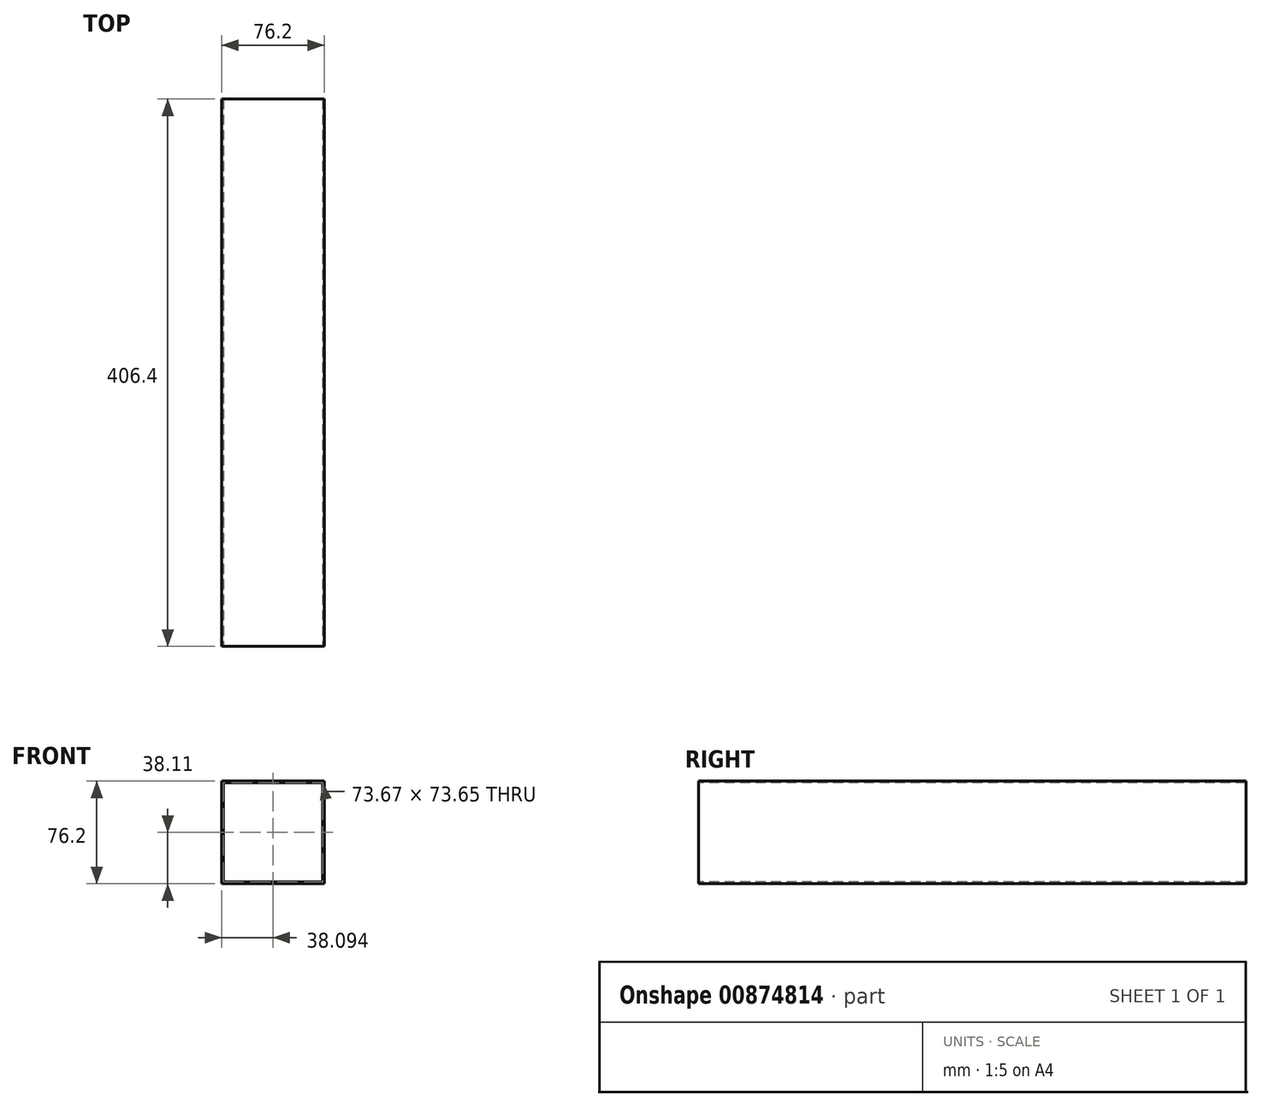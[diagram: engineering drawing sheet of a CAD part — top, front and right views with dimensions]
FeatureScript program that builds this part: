
annotation { "Feature Type Name" : "Feature", "Feature Type Description" : "" }
export const myFeature = defineFeature(function(context is Context, id is Id, definition is map)
    precondition{}
    {
        {
            var Q0;
            Q0=qCreatedBy(makeId("Front.planeOp"),FACE);
            var sketch = newSketch(context, id + "F0", { "sketchPlane" : qUnion([Q0])});
            skLineSegment(sketch, "E0.bottom", {"start": v(-117.25, 89.57) * mm, "end": v(-41.05, 89.57) * mm});
            skLineSegment(sketch, "E0.top", {"start": v(-117.25, 13.37) * mm, "end": v(-41.05, 13.37) * mm});
            skLineSegment(sketch, "E0.left", {"start": v(-117.25, 89.57) * mm, "end": v(-117.25, 13.37) * mm});
            skLineSegment(sketch, "E0.right", {"start": v(-41.05, 89.57) * mm, "end": v(-41.05, 13.37) * mm});
            skSolve(sketch);
        }
        {
            var Q0;
            Q0=qSketchRegion(id+"F0",true);
            extrude(context, id + "F1", {"entities" : qUnion([Q0]), "depth" : 609.6 * mm, "offsetDistance" : 25.4 * mm});
        }
        {
            var Q0;
            Q0=makeQuery(id+"F1.opExtrude","CAP_FACE",FACE,{"disambiguationData":[OSD([sQuery(id+"F0.wireOp",EDGE,"E0.bottom"),sQuery(id+"F0.wireOp",EDGE,"E0.top"),sQuery(id+"F0.wireOp",EDGE,"E0.left"),sQuery(id+"F0.wireOp",EDGE,"E0.right")])],"isStart":false});
            var sketch = newSketch(context, id + "F2", { "sketchPlane" : qUnion([Q0])});
            skLineSegment(sketch, "E1", {"start": v(-98.69, 89.57) * mm, "end": v(-98.69, 88.3) * mm});
            skLineSegment(sketch, "E2", {"start": v(-98.69, 88.3) * mm, "end": v(-116, 88.3) * mm});
            skLineSegment(sketch, "E3", {"start": v(-116, 88.3) * mm, "end": v(-116, 14.66) * mm});
            skLineSegment(sketch, "E4", {"start": v(-116, 14.66) * mm, "end": v(-42.32, 14.66) * mm});
            skLineSegment(sketch, "E5", {"start": v(-42.32, 14.66) * mm, "end": v(-42.32, 88.3) * mm});
            skLineSegment(sketch, "E6", {"start": v(-42.32, 88.3) * mm, "end": v(-98.69, 88.3) * mm});
            skSolve(sketch);
        }
        {
            var Q0;
            Q0=makeQuery(id+"F2.imprint","IMPRINT",FACE,{"disambiguationData":[TD([[makeQuery(id+"F2.imprint","IMPRINT",EDGE,{"derivedFrom":sQuery(id+"F2.wireOp",EDGE,"E2")}),1.0]])]});
            extrude(context, id + "F3", {"entities" : qUnion([Q0]), "operationType" : NewBodyOperationType.REMOVE, "oppositeDirection" : true, "depth" : 914.4 * mm, "offsetDistance" : 25.4 * mm});
        }
        {
            var Q0;
            Q0=makeQuery(id+"F1.opExtrude","CAP_FACE",FACE,{"disambiguationData":[OSD([sQuery(id+"F0.wireOp",EDGE,"E0.bottom"),sQuery(id+"F0.wireOp",EDGE,"E0.top"),sQuery(id+"F0.wireOp",EDGE,"E0.left"),sQuery(id+"F0.wireOp",EDGE,"E0.right")])],"isStart":false});
            extrude(context, id + "F4", {"entities" : qUnion([Q0]), "operationType" : NewBodyOperationType.ADD, "depth" : 304.8 * mm, "offsetDistance" : 25.4 * mm});
        }
        {
            var Q0;
            Q0=makeQuery(id+"F1.opExtrude","CAP_FACE",FACE,{"disambiguationData":[OSD([sQuery(id+"F0.wireOp",EDGE,"E0.bottom"),sQuery(id+"F0.wireOp",EDGE,"E0.top"),sQuery(id+"F0.wireOp",EDGE,"E0.left"),sQuery(id+"F0.wireOp",EDGE,"E0.right")])],"isStart":true});
            extrude(context, id + "F5", {"entities" : qUnion([Q0]), "operationType" : NewBodyOperationType.REMOVE, "oppositeDirection" : true, "depth" : 508 * mm, "offsetDistance" : 25.4 * mm});
        }
    });
